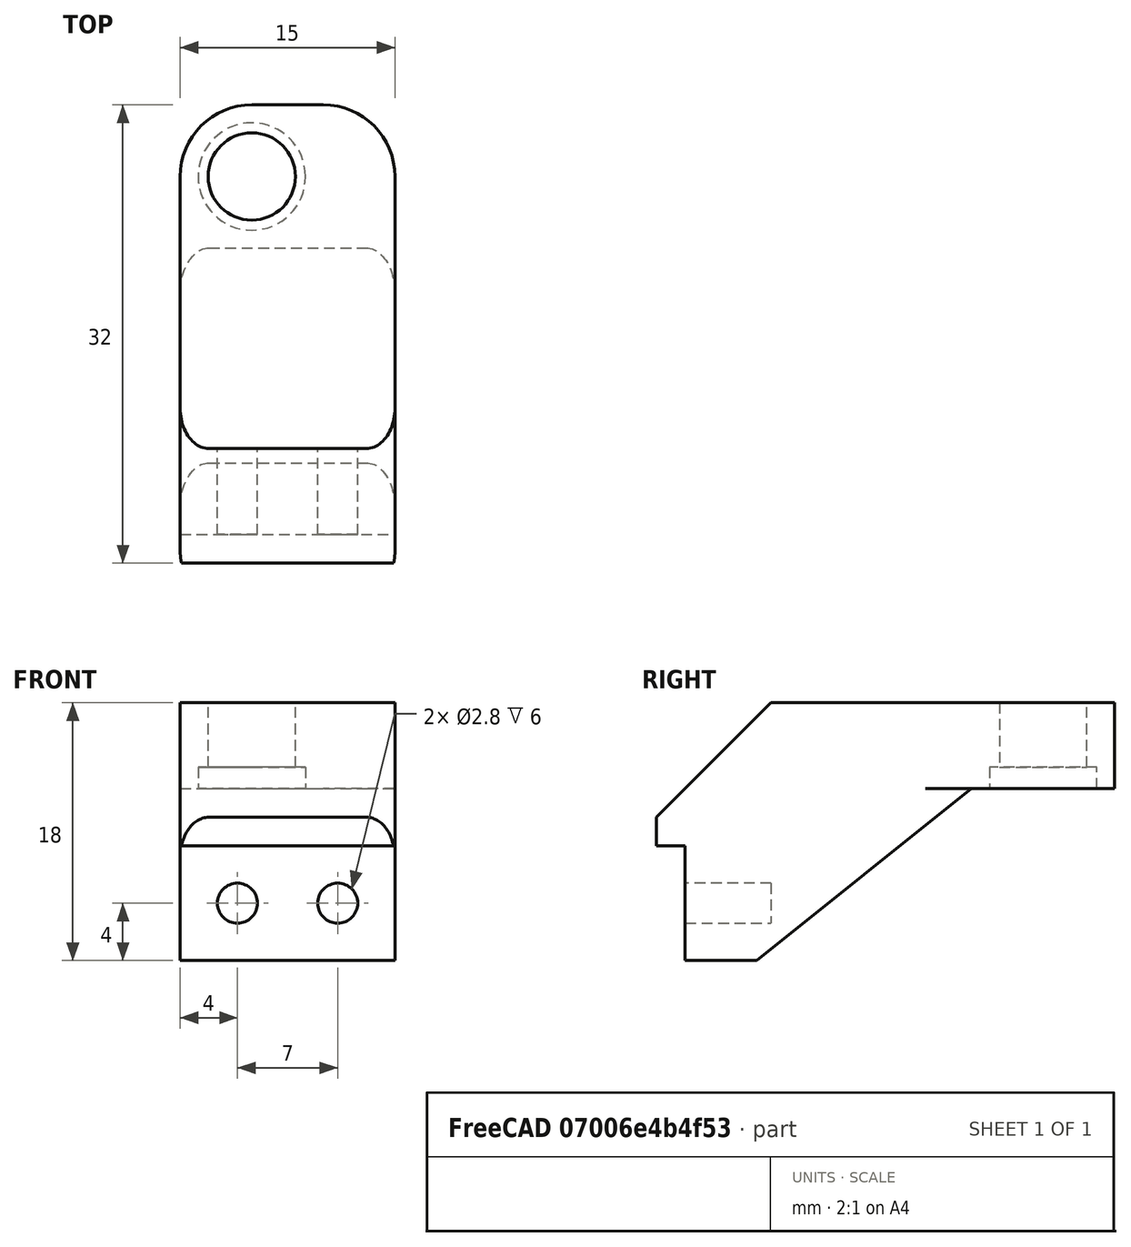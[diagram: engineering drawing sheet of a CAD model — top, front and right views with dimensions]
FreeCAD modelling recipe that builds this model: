
FCSTD DOCUMENT  (FreeCAD 0.19R)
Label: MicrometerHolder2
License: All rights reserved
LicenseURL: http://en.wikipedia.org/wiki/All_rights_reserved
objects: Sketcher::SketchObject×8, PartDesign::Pocket×5, PartDesign::Fillet×3, PartDesign::Pad×1, PartDesign::Body×1, Mesh::Feature×1
note: 27 computed .brp shape members not serialized (recipe doc carries the construction recipe); baked Part::Feature solids carry a one-line shape summary decoded from their .brp

FEATURE [Sketcher::SketchObject] Sketch
  FullyConstrained = true
  MapMode = 5
  Placement = pos=(0,0,0) rot=(0.57735,0.57735,0.57735;2.0944rad)
  Support = -> [YZ_Plane]
  sketch-geometry (9):
    g0: LineSegment StartX=6 StartY=0 StartZ=0 EndX=30 EndY=0 EndZ=0
    g1: LineSegment StartX=30 StartY=0 StartZ=0 EndX=30 EndY=-6 EndZ=0
    g2: LineSegment StartX=30 StartY=-6 StartZ=0 EndX=20 EndY=-6 EndZ=0
    g3: LineSegment StartX=5 StartY=-18 StartZ=0 EndX=0 EndY=-18 EndZ=0
    g4: LineSegment StartX=5 StartY=-18 StartZ=0 EndX=20 EndY=-6 EndZ=0
    g5: LineSegment StartX=-2 StartY=-8 StartZ=0 EndX=6 EndY=0 EndZ=0
    g6: LineSegment StartX=-2 StartY=-10 StartZ=0 EndX=-2 EndY=-8 EndZ=0
    g7: LineSegment StartX=-2 StartY=-10 StartZ=0 EndX=0 EndY=-10 EndZ=0
    g8: LineSegment StartX=0 StartY=-10 StartZ=0 EndX=0 EndY=-18 EndZ=0
  constraints (27):
    c: PointOnObject(g0,g-1)
    c: Coincident(g0,g1)
    c: Vertical(g1)
    c: Coincident(g1,g2)
    c: Horizontal(g2)
    c: PointOnObject(g3,g-2)
    c: Horizontal(g3)
    c: Distance(g3) = 5
    c: Distance(g1) = 6
    c: DistanceX(g0) = 30
    c: DistanceY(g3) = -18
    c: Coincident(g4,g2)
    c: Coincident(g0,g5)
    c: PointOnObject(g0,g-1)
    c: Angle(g5) = 0.785398
    c: Coincident(g4,g3)
    c: Coincident(g6,g5)
    c: Vertical(g6)
    c: DistanceX(g5) = -2
    c: Coincident(g6,g7)
    c: PointOnObject(g7,g-2)
    c: Horizontal(g7)
    c: Coincident(g7,g8)
    c: Coincident(g8,g3)
    c: Distance(g6) = 2
    c: Distance(g8) = 8
    c: DistanceX(g2) = 20
FEATURE [PartDesign::Pad] Pad
  Direction = (1,1,1)
  Length = 15
  Length2 = 100
  Placement = pos=(0,0,0) rot=(0.57735,0.57735,0.57735;2.0944rad)
  Profile = -> Sketch
  Type = 0
FEATURE [Sketcher::SketchObject] Sketch001
  FullyConstrained = true
  MapMode = 5
  Placement = pos=(1.32e-14,30,-6.6e-15) rot=(0.57735,0.57735,0.57735;4.18879rad)
  Support = -> [Pad]
  sketch-geometry (1):
    g0: Circle CenterX=-32 CenterY=7.5 CenterZ=0 NormalX=0 NormalY=0 NormalZ=1 AngleXU=0 Radius=4.725
  constraints (3):
    c: DistanceY(g0) = 7.5
    c: Diameter(g0) = 9.45
    c: DistanceX(g0) = -32
FEATURE [PartDesign::Pocket] Pocket
  BaseFeature = -> Pad
  Length = 5
  Length2 = 100
  Placement = pos=(0,0,0) rot=(0.57735,0.57735,0.57735;2.0944rad)
  Profile = -> Sketch001
  Type = 1
FEATURE [Sketcher::SketchObject] Sketch002
  FullyConstrained = false
  MapMode = 5
  Placement = pos=(0,0,0) rot=(-0.57735,-0.57735,0.57735;4.18879rad)
  Support = -> [Pocket]
  sketch-geometry (4):
    g0: LineSegment StartX=-28.5714 StartY=8.5 StartZ=0 EndX=-15.0736 EndY=8.5 EndZ=0
    g1: LineSegment StartX=-15.0736 StartY=8.5 StartZ=0 EndX=-15.0736 EndY=6.5 EndZ=0
    g2: LineSegment StartX=-15.0736 StartY=6.5 StartZ=0 EndX=-28.5714 EndY=6.5 EndZ=0
    g3: LineSegment StartX=-28.5714 StartY=6.5 StartZ=0 EndX=-28.5714 EndY=8.5 EndZ=0
  constraints (10):
    c: Coincident(g0,g1)
    c: Coincident(g1,g2)
    c: Coincident(g2,g3)
    c: Coincident(g3,g0)
    c: Horizontal(g0)
    c: Horizontal(g2)
    c: Vertical(g1)
    c: Vertical(g3)
    c: DistanceY(g1) = 6.5
    c: DistanceY(g0) = 8.5
FEATURE [PartDesign::Pocket] Pocket001
  BaseFeature = -> Pocket
  Length = 5
  Length2 = 100
  Placement = pos=(0,0,0) rot=(0.57735,0.57735,0.57735;2.0944rad)
  Profile = -> Sketch002
  Type = 1
FEATURE [Sketcher::SketchObject] Sketch011  label="clampthread"
  FullyConstrained = true
  MapMode = 5
  Placement = pos=(15,-1e-14,7e-15) rot=(0.57735,0.57735,0.57735;2.0944rad)
  sketch-geometry (1):
    g0: Circle CenterX=18 CenterY=-3 CenterZ=0 NormalX=0 NormalY=0 NormalZ=1 AngleXU=0 Radius=1.75
  constraints (3):
    c: Diameter(g0) = 3.5
    c: DistanceY(g0) = -3
    c: DistanceX(g0) = 18
FEATURE [Sketcher::SketchObject] Sketch012  label="ClampClearance"
  FullyConstrained = true
  MapMode = 5
  Placement = pos=(-8e-15,0,0) rot=(0.57735,0.57735,-0.57735;4.18879rad)
  sketch-geometry (1):
    g0: Circle CenterX=18 CenterY=3 CenterZ=0 NormalX=0 NormalY=0 NormalZ=1 AngleXU=0 Radius=1.4
  constraints (3):
    c: Diameter(g0) = 2.8
    c: DistanceY(g0) = 3
    c: DistanceX(g0) = 18
FEATURE [Sketcher::SketchObject] Sketch013  label="keyhole"
  FullyConstrained = false
  MapMode = 5
  Placement = pos=(0,0,-4e-15) rot=(0,0,-1;1.5708rad)
  sketch-geometry (2):
    g0: ArcOfCircle CenterX=-25 CenterY=5 CenterZ=0 NormalX=0 NormalY=0 NormalZ=1 AngleXU=0 Radius=3.05 StartAngle=6.09461 EndAngle=12.3778
    g1: Circle CenterX=-25 CenterY=5 CenterZ=0 NormalX=0 NormalY=0 NormalZ=1 AngleXU=0 Radius=3.05
  constraints (6):
    c: Diameter(g0) = 6.1
    c: DistanceY(g0) = 5
    c: DistanceX(g0) = -25
    c: Coincident(g0,g0)
    c: Coincident(g1,g0)
    c: Diameter(g1) = 6.1
FEATURE [Sketcher::SketchObject] Sketch014  label="screwholes"
  FullyConstrained = false
  MapMode = 5
  Placement = pos=(4e-15,6,-9e-15) rot=(0.57735,0.57735,0.57735;4.18879rad)
  sketch-geometry (3):
    g0: Circle CenterX=-14 CenterY=11 CenterZ=0 NormalX=0 NormalY=0 NormalZ=1 AngleXU=0 Radius=1.4
    g1: Circle CenterX=-14 CenterY=4 CenterZ=0 NormalX=0 NormalY=0 NormalZ=1 AngleXU=0 Radius=1.4
    g2: LineSegment StartX=-27.3 StartY=7.5 StartZ=0 EndX=12.2106 EndY=7.5 EndZ=0
  constraints (6):
    c: Diameter(g1) = 2.8
    c: Equal(g1,g0)
    c: DistanceX(g0,g1) = 0
    c: Distance(g0,g1) = 7
    c: DistanceY(g2) = 7.5
    c: Symmetric(g1,g0,g2)
FEATURE [Sketcher::SketchObject] Sketch015
  FullyConstrained = true
  MapMode = 5
  Placement = pos=(1.7e-15,-4e-15,-6) rot=(0.707107,0.707107,0;3.14159rad)
  sketch-geometry (1):
    g0: Circle CenterX=25 CenterY=5 CenterZ=0 NormalX=0 NormalY=0 NormalZ=1 AngleXU=0 Radius=3.75
  constraints (3):
    c: Diameter(g0) = 7.5
    c: DistanceX(g0) = 25
    c: DistanceY(g0) = 5
FEATURE [PartDesign::Pocket] Pocket002
  BaseFeature = -> Pocket001
  Length = 1.5
  Length2 = 100
  Placement = pos=(0,0,0) rot=(0.57735,0.57735,0.57735;2.0944rad)
  Profile = -> Sketch015
  Type = 0
FEATURE [PartDesign::Pocket] Pocket003
  BaseFeature = -> Pocket002
  Length = 5
  Length2 = 100
  Placement = pos=(0,0,0) rot=(0.57735,0.57735,0.57735;2.0944rad)
  Profile = -> Sketch013
  Type = 0
FEATURE [PartDesign::Pocket] Pocket004
  BaseFeature = -> Pocket003
  Length = 11
  Length2 = 100
  Placement = pos=(0,0,0) rot=(0.57735,0.57735,0.57735;2.0944rad)
  Profile = -> Sketch014
  Type = 0
FEATURE [PartDesign::Fillet] Fillet
  Base = -> Pocket004 [Edge18,Edge12]
  BaseFeature = -> Pocket004
  Placement = pos=(0,0,0) rot=(0.57735,0.57735,0.57735;2.0944rad)
  Radius = 5
  SupportTransform = false
FEATURE [PartDesign::Fillet] Fillet001
  Base = -> Fillet [Edge19,Edge3]
  BaseFeature = -> Fillet
  Placement = pos=(0,0,0) rot=(0.57735,0.57735,0.57735;2.0944rad)
  Radius = 2
  SupportTransform = false
FEATURE [PartDesign::Fillet] Fillet002
  Base = -> Fillet001 [Edge36,Edge7]
  BaseFeature = -> Fillet001
  Placement = pos=(0,0,0) rot=(0.57735,0.57735,0.57735;2.0944rad)
  Radius = 2
  SupportTransform = false
FEATURE [PartDesign::Body] Body
  Group = -> [Sketch,Pad,Sketch001,Pocket,Sketch002,Pocket001,Sketch011,Sketch012,Sketch013,Sketch014,Sketch015,Pocket002,Pocket003,Pocket004,Fillet,Fillet001,Fillet002]
  Origin = -> Origin
  Tip = -> Fillet002
FEATURE [Mesh::Feature] Mesh  label="Fillet002 (Meshed)"
